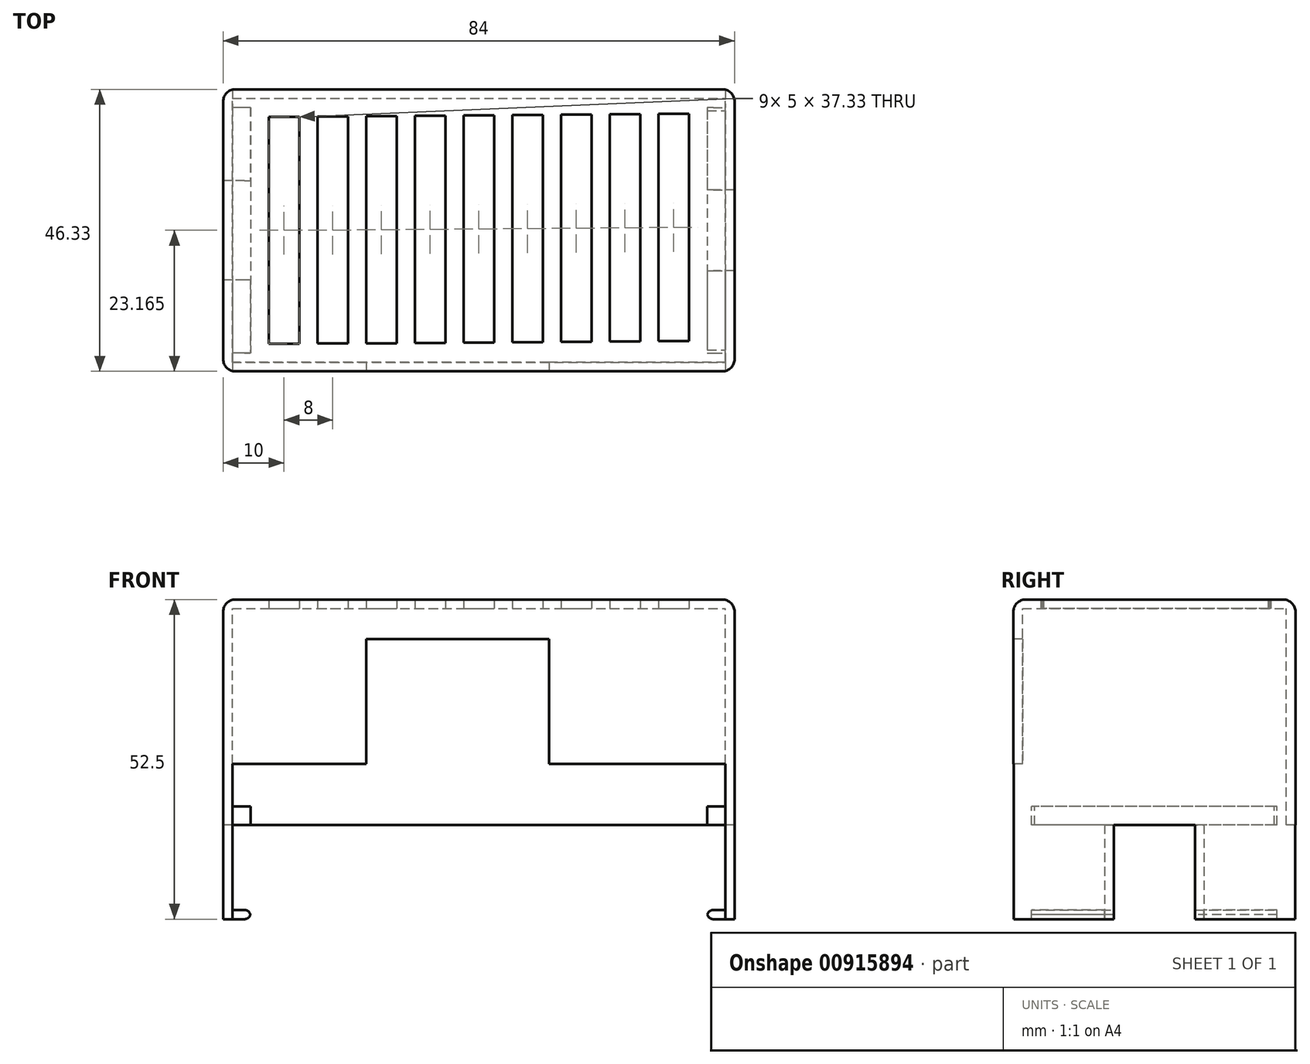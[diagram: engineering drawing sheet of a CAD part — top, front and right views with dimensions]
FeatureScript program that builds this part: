
annotation { "Feature Type Name" : "Feature", "Feature Type Description" : "" }
export const myFeature = defineFeature(function(context is Context, id is Id, definition is map)
    precondition{}
    {
        {
            var Q0;
            Q0=qCreatedBy(makeId("Top.planeOp"),FACE);
            var sketch = newSketch(context, id + "F0", { "sketchPlane" : qUnion([Q0])});
            skLineSegment(sketch, "E0.bottom", {"start": v(0, 0) * mm, "end": v(84, 0) * mm});
            skLineSegment(sketch, "E0.top", {"start": v(0, 46.33) * mm, "end": v(84, 46.33) * mm});
            skLineSegment(sketch, "E0.left", {"start": v(0, 0) * mm, "end": v(0, 46.33) * mm});
            skLineSegment(sketch, "E0.right", {"start": v(84, 0) * mm, "end": v(84, 46.33) * mm});
            skSolve(sketch);
        }
        {
            var Q0;
            Q0=makeQuery(id+"F0.imprint","IMPRINT",FACE,{"disambiguationData":[TD([[makeQuery(id+"F0.imprint","IMPRINT",EDGE,{"derivedFrom":sQuery(id+"F0.wireOp",EDGE,"E0.bottom")}),1.0]])]});
            extrude(context, id + "F1", {"entities" : qUnion([Q0]), "oppositeDirection" : true, "depth" : 37 * mm, "offsetDistance" : 25 * mm});
        }
        {
            var Q0;
            Q0=makeQuery(id+"F1.opExtrude","CAP_FACE",FACE,{"disambiguationData":[OSD([sQuery(id+"F0.wireOp",EDGE,"E0.bottom"),sQuery(id+"F0.wireOp",EDGE,"E0.top"),sQuery(id+"F0.wireOp",EDGE,"E0.left"),sQuery(id+"F0.wireOp",EDGE,"E0.right")])],"isStart":false});
            shell(context, id + "F2", {"entities" : qUnion([Q0]), "thickness" : 1.5 * mm});
        }
        {
            var Q0;
            Q0=makeQuery(id+"F1.opExtrude","SWEPT_FACE",FACE,{"disambiguationData":[OSD([sQuery(id+"F0.wireOp",EDGE,"E0.top")])]});
            var sketch = newSketch(context, id + "F3", { "sketchPlane" : qUnion([Q0])});
            skLineSegment(sketch, "E1.bottom", {"start": v(-82.5, -37) * mm, "end": v(-1.5, -37) * mm});
            skLineSegment(sketch, "E1.top", {"start": v(-82.5, -1.5) * mm, "end": v(-1.5, -1.5) * mm});
            skLineSegment(sketch, "E1.left", {"start": v(-82.5, -37) * mm, "end": v(-82.5, -1.5) * mm});
            skLineSegment(sketch, "E1.right", {"start": v(-1.5, -37) * mm, "end": v(-1.5, -1.5) * mm});
            skSolve(sketch);
        }
        {
            var Q0;
            Q0=makeQuery(id+"F1.opExtrude","SWEPT_FACE",FACE,{"disambiguationData":[OSD([sQuery(id+"F0.wireOp",EDGE,"E0.bottom")])]});
            var sketch = newSketch(context, id + "F4", { "sketchPlane" : qUnion([Q0])});
            skLineSegment(sketch, "E2.bottom", {"start": v(1.5, -37) * mm, "end": v(82.5, -37) * mm});
            skLineSegment(sketch, "E2.top", {"start": v(1.5, -27) * mm, "end": v(82.5, -27) * mm});
            skLineSegment(sketch, "E2.left", {"start": v(1.5, -37) * mm, "end": v(1.5, -27) * mm});
            skLineSegment(sketch, "E2.right", {"start": v(82.5, -37) * mm, "end": v(82.5, -27) * mm});
            skSolve(sketch);
        }
        {
            var Q0;
            Q0=makeQuery(id+"F4.imprint","IMPRINT",FACE,{"disambiguationData":[TD([[makeQuery(id+"F4.imprint","IMPRINT",EDGE,{"derivedFrom":sQuery(id+"F4.wireOp",EDGE,"E2.bottom")}),1.0]])]});
            extrude(context, id + "F5", {"entities" : qUnion([Q0]), "operationType" : NewBodyOperationType.REMOVE, "endBound" : BoundingType.UP_TO_NEXT, "oppositeDirection" : true, "depth" : 25 * mm, "offsetDistance" : 25 * mm});
        }
        {
            var Q0;
            Q0=makeQuery(id+"F1.opExtrude","SWEPT_FACE",FACE,{"disambiguationData":[OSD([sQuery(id+"F0.wireOp",EDGE,"E0.bottom")])]});
            var sketch = newSketch(context, id + "F6", { "sketchPlane" : qUnion([Q0])});
            skLineSegment(sketch, "E3.bottom", {"start": v(23.5, -27) * mm, "end": v(53.5, -27) * mm});
            skLineSegment(sketch, "E3.top", {"start": v(23.5, -6.5) * mm, "end": v(53.5, -6.5) * mm});
            skLineSegment(sketch, "E3.left", {"start": v(23.5, -27) * mm, "end": v(23.5, -6.5) * mm});
            skLineSegment(sketch, "E3.right", {"start": v(53.5, -27) * mm, "end": v(53.5, -6.5) * mm});
            skSolve(sketch);
        }
        {
            var Q0;
            Q0=makeQuery(id+"F6.imprint","IMPRINT",FACE,{"disambiguationData":[TD([[makeQuery(id+"F6.imprint","IMPRINT",EDGE,{"derivedFrom":sQuery(id+"F6.wireOp",EDGE,"E3.bottom")}),1.0]])]});
            extrude(context, id + "F7", {"entities" : qUnion([Q0]), "operationType" : NewBodyOperationType.REMOVE, "endBound" : BoundingType.UP_TO_NEXT, "oppositeDirection" : true, "depth" : 25 * mm, "offsetDistance" : 25 * mm});
        }
        {
            var Q0;
            Q0=makeQuery(id+"F1.opExtrude","CAP_FACE",FACE,{"disambiguationData":[OSD([sQuery(id+"F0.wireOp",EDGE,"E0.bottom"),sQuery(id+"F0.wireOp",EDGE,"E0.top"),sQuery(id+"F0.wireOp",EDGE,"E0.left"),sQuery(id+"F0.wireOp",EDGE,"E0.right")])],"isStart":false});
            var sketch = newSketch(context, id + "F8", { "sketchPlane" : qUnion([Q0])});
            skLineSegment(sketch, "E4.bottom", {"start": v(0, -46.33) * mm, "end": v(1.5, -46.33) * mm});
            skLineSegment(sketch, "E4.top", {"start": v(0, 0) * mm, "end": v(1.5, 0) * mm});
            skLineSegment(sketch, "E4.left", {"start": v(0, -46.33) * mm, "end": v(0, 0) * mm});
            skLineSegment(sketch, "E4.right", {"start": v(1.5, -46.33) * mm, "end": v(1.5, 0) * mm});
            skLineSegment(sketch, "E5.bottom", {"start": v(84, -46.33) * mm, "end": v(82.5, -46.33) * mm});
            skLineSegment(sketch, "E5.top", {"start": v(84, 0) * mm, "end": v(82.5, 0) * mm});
            skLineSegment(sketch, "E5.left", {"start": v(84, -46.33) * mm, "end": v(84, 0) * mm});
            skLineSegment(sketch, "E5.right", {"start": v(82.5, -46.33) * mm, "end": v(82.5, 0) * mm});
            skSolve(sketch);
        }
        {
            var Q0;
            {var subQ4=sQuery(id+"F8.wireOp",EDGE,"E4.bottom");Q0=makeQuery(id+"F8.imprint","IMPRINT",FACE,{"disambiguationData":[TD([[makeQuery(id+"F8.imprint","IMPRINT",EDGE,{"derivedFrom":subQ4}),1.0]])]});}
            var Q1;
            {var subQ4=sQuery(id+"F8.wireOp",EDGE,"E5.bottom");Q1=makeQuery(id+"F8.imprint","IMPRINT",FACE,{"disambiguationData":[TD([[makeQuery(id+"F8.imprint","IMPRINT",EDGE,{"derivedFrom":subQ4}),1.0]])]});}
            extrude(context, id + "F9", {"entities" : qUnion([Q0, Q1]), "operationType" : NewBodyOperationType.ADD, "depth" : 15.5 * mm, "offsetDistance" : 25 * mm});
        }
        {
            var Q0;
            Q0=makeQuery(id+"F9.boolean.opBoolean","MERGE",FACE,{"derivedFrom":[makeQuery(id+"F5.boolean.opBoolean","MERGE",FACE,{"derivedFrom":[makeQuery(id+"F2.opShell","OFFSET_FACE",FACE,{"disambiguationData":[OSD([sQuery(id+"F0.wireOp",EDGE,"E0.left")])]})],"fromTools":[makeQuery(id+"F5.opExtrude","SWEPT_FACE",FACE,{"disambiguationData":[OSD([sQuery(id+"F4.wireOp",EDGE,"E2.left")])]})]}),makeQuery(id+"F9.opExtrude","SWEPT_FACE",FACE,{"disambiguationData":[OSD([sQuery(id+"F8.wireOp",EDGE,"E4.right")])]})]});
            var sketch = newSketch(context, id + "F10", { "sketchPlane" : qUnion([Q0])});
            skLineSegment(sketch, "E6.bottom", {"start": v(43.33, -37) * mm, "end": v(3, -37) * mm});
            skLineSegment(sketch, "E6.top", {"start": v(43.33, -34) * mm, "end": v(3, -34) * mm});
            skLineSegment(sketch, "E6.left", {"start": v(43.33, -37) * mm, "end": v(43.33, -34) * mm});
            skLineSegment(sketch, "E6.right", {"start": v(3, -37) * mm, "end": v(3, -34) * mm});
            skSolve(sketch);
        }
        {
            var Q0;
            Q0=makeQuery(id+"F10.imprint","IMPRINT",FACE,{"disambiguationData":[TD([[makeQuery(id+"F10.imprint","IMPRINT",EDGE,{"derivedFrom":sQuery(id+"F10.wireOp",EDGE,"E6.bottom")}),-1.0]])]});
            extrude(context, id + "F11", {"entities" : qUnion([Q0]), "operationType" : NewBodyOperationType.ADD, "depth" : 3 * mm, "offsetDistance" : 25 * mm});
        }
        {
            var Q0;
            Q0=makeQuery(id+"F9.boolean.opBoolean","MERGE",FACE,{"derivedFrom":[makeQuery(id+"F5.boolean.opBoolean","MERGE",FACE,{"derivedFrom":[makeQuery(id+"F2.opShell","OFFSET_FACE",FACE,{"disambiguationData":[OSD([sQuery(id+"F0.wireOp",EDGE,"E0.right")])]})],"fromTools":[makeQuery(id+"F5.opExtrude","SWEPT_FACE",FACE,{"disambiguationData":[OSD([sQuery(id+"F4.wireOp",EDGE,"E2.right")])]})]}),makeQuery(id+"F9.opExtrude","SWEPT_FACE",FACE,{"disambiguationData":[OSD([sQuery(id+"F8.wireOp",EDGE,"E5.right")])]})]});
            var sketch = newSketch(context, id + "F12", { "sketchPlane" : qUnion([Q0])});
            skLineSegment(sketch, "E7.bottom", {"start": v(-42.83, -37) * mm, "end": v(-3.5, -37) * mm});
            skLineSegment(sketch, "E7.top", {"start": v(-42.83, -34) * mm, "end": v(-3.5, -34) * mm});
            skLineSegment(sketch, "E7.left", {"start": v(-42.83, -37) * mm, "end": v(-42.83, -34) * mm});
            skLineSegment(sketch, "E7.right", {"start": v(-3.5, -37) * mm, "end": v(-3.5, -34) * mm});
            skSolve(sketch);
        }
        {
            var Q0;
            Q0=makeQuery(id+"F12.imprint","IMPRINT",FACE,{"disambiguationData":[TD([[makeQuery(id+"F12.imprint","IMPRINT",EDGE,{"derivedFrom":sQuery(id+"F12.wireOp",EDGE,"E7.bottom")}),1.0]])]});
            extrude(context, id + "F13", {"entities" : qUnion([Q0]), "operationType" : NewBodyOperationType.ADD, "depth" : 3 * mm, "offsetDistance" : 25 * mm});
        }
        {
            var Q0;
            Q0=makeQuery(id+"F9.opExtrude","CAP_FACE",FACE,{"disambiguationData":[OSD([sQuery(id+"F8.wireOp",EDGE,"E5.bottom"),sQuery(id+"F8.wireOp",EDGE,"E5.top"),sQuery(id+"F8.wireOp",EDGE,"E5.left"),sQuery(id+"F8.wireOp",EDGE,"E5.right")])],"isStart":false});
            var sketch = newSketch(context, id + "F14", { "sketchPlane" : qUnion([Q0])});
            skLineSegment(sketch, "E8.bottom", {"start": v(84, -29.83) * mm, "end": v(82.5, -29.83) * mm});
            skLineSegment(sketch, "E8.top", {"start": v(84, -16.5) * mm, "end": v(82.5, -16.5) * mm});
            skLineSegment(sketch, "E8.left", {"start": v(84, -29.83) * mm, "end": v(84, -16.5) * mm});
            skLineSegment(sketch, "E8.right", {"start": v(82.5, -29.83) * mm, "end": v(82.5, -16.5) * mm});
            skSolve(sketch);
        }
        {
            var Q0;
            Q0=makeQuery(id+"F14.imprint","IMPRINT",FACE,{"disambiguationData":[TD([[makeQuery(id+"F14.imprint","IMPRINT",EDGE,{"derivedFrom":sQuery(id+"F14.wireOp",EDGE,"E8.bottom")}),-1.0]])]});
            extrude(context, id + "F15", {"entities" : qUnion([Q0]), "operationType" : NewBodyOperationType.REMOVE, "oppositeDirection" : true, "depth" : 15.5 * mm, "offsetDistance" : 25 * mm});
        }
        {
            var Q0;
            Q0=makeQuery(id+"F9.opExtrude","CAP_FACE",FACE,{"disambiguationData":[OSD([sQuery(id+"F8.wireOp",EDGE,"E4.bottom"),sQuery(id+"F8.wireOp",EDGE,"E4.top"),sQuery(id+"F8.wireOp",EDGE,"E4.left"),sQuery(id+"F8.wireOp",EDGE,"E4.right")])],"isStart":false});
            var sketch = newSketch(context, id + "F16", { "sketchPlane" : qUnion([Q0])});
            skLineSegment(sketch, "E9.bottom", {"start": v(1.5, -31.33) * mm, "end": v(0, -31.33) * mm});
            skLineSegment(sketch, "E9.top", {"start": v(1.5, -15) * mm, "end": v(0, -15) * mm});
            skLineSegment(sketch, "E9.left", {"start": v(1.5, -31.33) * mm, "end": v(1.5, -15) * mm});
            skLineSegment(sketch, "E9.right", {"start": v(0, -31.33) * mm, "end": v(0, -15) * mm});
            skSolve(sketch);
        }
        {
            var Q0;
            Q0=makeQuery(id+"F16.imprint","IMPRINT",FACE,{"disambiguationData":[TD([[makeQuery(id+"F16.imprint","IMPRINT",EDGE,{"derivedFrom":sQuery(id+"F16.wireOp",EDGE,"E9.bottom")}),-1.0]])]});
            extrude(context, id + "F17", {"entities" : qUnion([Q0]), "operationType" : NewBodyOperationType.REMOVE, "oppositeDirection" : true, "depth" : 15.5 * mm, "offsetDistance" : 25 * mm});
        }
        {
            var Q0;
            Q0=makeQuery(id+"F9.boolean.opBoolean","MERGE",FACE,{"derivedFrom":[makeQuery(id+"F5.boolean.opBoolean","MERGE",FACE,{"derivedFrom":[makeQuery(id+"F2.opShell","OFFSET_FACE",FACE,{"disambiguationData":[OSD([sQuery(id+"F0.wireOp",EDGE,"E0.left")])]})],"fromTools":[makeQuery(id+"F5.opExtrude","SWEPT_FACE",FACE,{"disambiguationData":[OSD([sQuery(id+"F4.wireOp",EDGE,"E2.left")])]})]}),makeQuery(id+"F9.opExtrude","SWEPT_FACE",FACE,{"disambiguationData":[OSD([sQuery(id+"F8.wireOp",EDGE,"E4.right")])]})]});
            var sketch = newSketch(context, id + "F18", { "sketchPlane" : qUnion([Q0])});
            skLineSegment(sketch, "E10.bottom", {"start": v(43.33, -52.5) * mm, "end": v(31.33, -52.5) * mm});
            skLineSegment(sketch, "E10.top", {"start": v(43.33, -51) * mm, "end": v(31.33, -51) * mm});
            skLineSegment(sketch, "E10.left", {"start": v(43.33, -52.5) * mm, "end": v(43.33, -51) * mm});
            skLineSegment(sketch, "E10.right", {"start": v(3, -52.5) * mm, "end": v(3, -51) * mm});
            skLineSegment(sketch, "E11", {"start": v(31.33, -52.5) * mm, "end": v(31.33, -51) * mm});
            skLineSegment(sketch, "E12", {"start": v(15, -52.5) * mm, "end": v(15, -51) * mm});
            skLineSegment(sketch, "E13.trimOffspring", {"start": v(15, -52.5) * mm, "end": v(3, -52.5) * mm});
            skLineSegment(sketch, "E14.trimOffspring", {"start": v(15, -51) * mm, "end": v(3, -51) * mm});
            skSolve(sketch);
        }
        {
            var Q0;
            Q0=makeQuery(id+"F18.imprint","IMPRINT",FACE,{"disambiguationData":[TD([[makeQuery(id+"F18.imprint","IMPRINT",EDGE,{"derivedFrom":sQuery(id+"F18.wireOp",EDGE,"E10.bottom")}),-1.0]])]});
            var Q1;
            Q1=makeQuery(id+"F18.imprint","IMPRINT",FACE,{"disambiguationData":[TD([[makeQuery(id+"F18.imprint","IMPRINT",EDGE,{"derivedFrom":sQuery(id+"F18.wireOp",EDGE,"E10.right")}),-1.0]])]});
            extrude(context, id + "F19", {"entities" : qUnion([Q0, Q1]), "operationType" : NewBodyOperationType.ADD, "depth" : 3 * mm, "offsetDistance" : 25 * mm});
        }
        {
            var Q0;
            Q0=makeQuery(id+"F9.boolean.opBoolean","MERGE",FACE,{"derivedFrom":[makeQuery(id+"F5.boolean.opBoolean","MERGE",FACE,{"derivedFrom":[makeQuery(id+"F2.opShell","OFFSET_FACE",FACE,{"disambiguationData":[OSD([sQuery(id+"F0.wireOp",EDGE,"E0.right")])]})],"fromTools":[makeQuery(id+"F5.opExtrude","SWEPT_FACE",FACE,{"disambiguationData":[OSD([sQuery(id+"F4.wireOp",EDGE,"E2.right")])]})]}),makeQuery(id+"F9.opExtrude","SWEPT_FACE",FACE,{"disambiguationData":[OSD([sQuery(id+"F8.wireOp",EDGE,"E5.right")])]})]});
            var sketch = newSketch(context, id + "F20", { "sketchPlane" : qUnion([Q0])});
            skLineSegment(sketch, "E15.bottom", {"start": v(-3, -52.5) * mm, "end": v(-16.5, -52.5) * mm});
            skLineSegment(sketch, "E15.top", {"start": v(-3, -51) * mm, "end": v(-16.5, -51) * mm});
            skLineSegment(sketch, "E15.left", {"start": v(-3, -52.5) * mm, "end": v(-3, -51) * mm});
            skLineSegment(sketch, "E15.right", {"start": v(-43.33, -52.5) * mm, "end": v(-43.33, -51) * mm});
            skLineSegment(sketch, "E16", {"start": v(-16.5, -52.5) * mm, "end": v(-16.5, -51) * mm});
            skLineSegment(sketch, "E17", {"start": v(-29.83, -52.5) * mm, "end": v(-29.83, -51) * mm});
            skLineSegment(sketch, "E18.trimOffspring", {"start": v(-29.83, -52.5) * mm, "end": v(-43.33, -52.5) * mm});
            skLineSegment(sketch, "E19.trimOffspring", {"start": v(-29.83, -51) * mm, "end": v(-43.33, -51) * mm});
            skSolve(sketch);
        }
        {
            var Q0;
            Q0=makeQuery(id+"F20.imprint","IMPRINT",FACE,{"disambiguationData":[TD([[makeQuery(id+"F20.imprint","IMPRINT",EDGE,{"derivedFrom":sQuery(id+"F20.wireOp",EDGE,"E15.bottom")}),1.0]])]});
            var Q1;
            Q1=makeQuery(id+"F20.imprint","IMPRINT",FACE,{"disambiguationData":[TD([[makeQuery(id+"F20.imprint","IMPRINT",EDGE,{"derivedFrom":sQuery(id+"F20.wireOp",EDGE,"E15.right")}),-1.0]])]});
            extrude(context, id + "F21", {"entities" : qUnion([Q0, Q1]), "operationType" : NewBodyOperationType.ADD, "depth" : 3 * mm, "offsetDistance" : 25 * mm});
        }
        {
            var Q0;
            Q0=makeQuery(id+"F2.opShell","OFFSET_FACE",FACE,{"disambiguationData":[OSD([sQuery(id+"F0.wireOp",EDGE,"E0.bottom"),sQuery(id+"F0.wireOp",EDGE,"E0.top"),sQuery(id+"F0.wireOp",EDGE,"E0.left"),sQuery(id+"F0.wireOp",EDGE,"E0.right")])]});
            var sketch = newSketch(context, id + "F22", { "sketchPlane" : qUnion([Q0])});
            skLineSegment(sketch, "E20.bottom", {"start": v(7.5, -41.83) * mm, "end": v(12.5, -41.83) * mm});
            skLineSegment(sketch, "E20.top", {"start": v(7.5, -4.5) * mm, "end": v(12.5, -4.5) * mm});
            skLineSegment(sketch, "E20.left", {"start": v(7.5, -41.83) * mm, "end": v(7.5, -4.5) * mm});
            skLineSegment(sketch, "E20.right", {"start": v(12.5, -41.83) * mm, "end": v(12.5, -4.5) * mm});
            skLineSegment(sketch, "E21.1.0.0", {"start": v(20.5, -41.89) * mm, "end": v(20.5, -4.56) * mm});
            skLineSegment(sketch, "E21.1.0.1", {"start": v(15.5, -4.56) * mm, "end": v(20.5, -4.56) * mm});
            skLineSegment(sketch, "E21.1.0.2", {"start": v(15.5, -41.89) * mm, "end": v(15.5, -4.56) * mm});
            skLineSegment(sketch, "E21.1.0.3", {"start": v(15.5, -41.89) * mm, "end": v(20.5, -41.89) * mm});
            skLineSegment(sketch, "E21.2.0.0", {"start": v(28.5, -41.95) * mm, "end": v(28.5, -4.62) * mm});
            skLineSegment(sketch, "E21.2.0.1", {"start": v(23.5, -4.62) * mm, "end": v(28.5, -4.62) * mm});
            skLineSegment(sketch, "E21.2.0.2", {"start": v(23.5, -41.95) * mm, "end": v(23.5, -4.62) * mm});
            skLineSegment(sketch, "E21.2.0.3", {"start": v(23.5, -41.95) * mm, "end": v(28.5, -41.95) * mm});
            skLineSegment(sketch, "E21.3.0.0", {"start": v(36.5, -42) * mm, "end": v(36.5, -4.68) * mm});
            skLineSegment(sketch, "E21.3.0.1", {"start": v(31.5, -4.68) * mm, "end": v(36.5, -4.68) * mm});
            skLineSegment(sketch, "E21.3.0.2", {"start": v(31.5, -42) * mm, "end": v(31.5, -4.68) * mm});
            skLineSegment(sketch, "E21.3.0.3", {"start": v(31.5, -42) * mm, "end": v(36.5, -42) * mm});
            skLineSegment(sketch, "E21.4.0.0", {"start": v(44.5, -42.07) * mm, "end": v(44.5, -4.74) * mm});
            skLineSegment(sketch, "E21.4.0.1", {"start": v(39.5, -4.74) * mm, "end": v(44.5, -4.74) * mm});
            skLineSegment(sketch, "E21.4.0.2", {"start": v(39.5, -42.07) * mm, "end": v(39.5, -4.74) * mm});
            skLineSegment(sketch, "E21.4.0.3", {"start": v(39.5, -42.07) * mm, "end": v(44.5, -42.07) * mm});
            skLineSegment(sketch, "E21.5.0.0", {"start": v(52.5, -42.13) * mm, "end": v(52.5, -4.8) * mm});
            skLineSegment(sketch, "E21.5.0.1", {"start": v(47.5, -4.8) * mm, "end": v(52.5, -4.8) * mm});
            skLineSegment(sketch, "E21.5.0.2", {"start": v(47.5, -42.13) * mm, "end": v(47.5, -4.8) * mm});
            skLineSegment(sketch, "E21.5.0.3", {"start": v(47.5, -42.13) * mm, "end": v(52.5, -42.13) * mm});
            skLineSegment(sketch, "E21.6.0.0", {"start": v(60.5, -42.19) * mm, "end": v(60.5, -4.86) * mm});
            skLineSegment(sketch, "E21.6.0.1", {"start": v(55.5, -4.86) * mm, "end": v(60.5, -4.86) * mm});
            skLineSegment(sketch, "E21.6.0.2", {"start": v(55.5, -42.19) * mm, "end": v(55.5, -4.86) * mm});
            skLineSegment(sketch, "E21.6.0.3", {"start": v(55.5, -42.19) * mm, "end": v(60.5, -42.19) * mm});
            skLineSegment(sketch, "E21.7.0.0", {"start": v(68.5, -42.25) * mm, "end": v(68.5, -4.92) * mm});
            skLineSegment(sketch, "E21.7.0.1", {"start": v(63.5, -4.92) * mm, "end": v(68.5, -4.92) * mm});
            skLineSegment(sketch, "E21.7.0.2", {"start": v(63.5, -42.25) * mm, "end": v(63.5, -4.92) * mm});
            skLineSegment(sketch, "E21.7.0.3", {"start": v(63.5, -42.25) * mm, "end": v(68.5, -42.25) * mm});
            skLineSegment(sketch, "E21.8.0.0", {"start": v(76.5, -42.3) * mm, "end": v(76.5, -4.98) * mm});
            skLineSegment(sketch, "E21.8.0.1", {"start": v(71.5, -4.98) * mm, "end": v(76.5, -4.98) * mm});
            skLineSegment(sketch, "E21.8.0.2", {"start": v(71.5, -42.3) * mm, "end": v(71.5, -4.98) * mm});
            skLineSegment(sketch, "E21.8.0.3", {"start": v(71.5, -42.3) * mm, "end": v(76.5, -42.3) * mm});
            skLineSegment(sketch, "E21.direction1", {"start": v(7.5, -41.83) * mm, "end": v(15.5, -41.89) * mm, "construction": true});
            skSolve(sketch);
        }
        {
            var Q0;
            Q0=makeQuery(id+"F22.imprint","IMPRINT",FACE,{"disambiguationData":[TD([[makeQuery(id+"F22.imprint","IMPRINT",EDGE,{"derivedFrom":sQuery(id+"F22.wireOp",EDGE,"E21.8.0.0")}),1.0]])]});
            var Q1;
            Q1=makeQuery(id+"F22.imprint","IMPRINT",FACE,{"disambiguationData":[TD([[makeQuery(id+"F22.imprint","IMPRINT",EDGE,{"derivedFrom":sQuery(id+"F22.wireOp",EDGE,"E21.7.0.0")}),1.0]])]});
            var Q2;
            Q2=makeQuery(id+"F22.imprint","IMPRINT",FACE,{"disambiguationData":[TD([[makeQuery(id+"F22.imprint","IMPRINT",EDGE,{"derivedFrom":sQuery(id+"F22.wireOp",EDGE,"E21.5.0.0")}),1.0]])]});
            var Q3;
            Q3=makeQuery(id+"F22.imprint","IMPRINT",FACE,{"disambiguationData":[TD([[makeQuery(id+"F22.imprint","IMPRINT",EDGE,{"derivedFrom":sQuery(id+"F22.wireOp",EDGE,"E21.4.0.0")}),1.0]])]});
            var Q4;
            Q4=makeQuery(id+"F22.imprint","IMPRINT",FACE,{"disambiguationData":[TD([[makeQuery(id+"F22.imprint","IMPRINT",EDGE,{"derivedFrom":sQuery(id+"F22.wireOp",EDGE,"E21.3.0.0")}),1.0]])]});
            var Q5;
            Q5=makeQuery(id+"F22.imprint","IMPRINT",FACE,{"disambiguationData":[TD([[makeQuery(id+"F22.imprint","IMPRINT",EDGE,{"derivedFrom":sQuery(id+"F22.wireOp",EDGE,"E21.2.0.0")}),1.0]])]});
            var Q6;
            Q6=makeQuery(id+"F22.imprint","IMPRINT",FACE,{"disambiguationData":[TD([[makeQuery(id+"F22.imprint","IMPRINT",EDGE,{"derivedFrom":sQuery(id+"F22.wireOp",EDGE,"E21.1.0.0")}),1.0]])]});
            var Q7;
            Q7=makeQuery(id+"F22.imprint","IMPRINT",FACE,{"disambiguationData":[TD([[makeQuery(id+"F22.imprint","IMPRINT",EDGE,{"derivedFrom":sQuery(id+"F22.wireOp",EDGE,"E20.bottom")}),1.0]])]});
            var Q8;
            Q8=makeQuery(id+"F22.imprint","IMPRINT",FACE,{"disambiguationData":[TD([[makeQuery(id+"F22.imprint","IMPRINT",EDGE,{"derivedFrom":sQuery(id+"F22.wireOp",EDGE,"E21.6.0.0")}),1.0]])]});
            extrude(context, id + "F23", {"entities" : qUnion([Q0, Q1, Q2, Q3, Q4, Q5, Q6, Q7, Q8]), "operationType" : NewBodyOperationType.REMOVE, "endBound" : BoundingType.UP_TO_NEXT, "oppositeDirection" : true, "depth" : 25 * mm, "offsetDistance" : 25 * mm});
        }
        {
            var Q0;
            Q0=makeQuery(id+"F1.opExtrude","CAP_EDGE",EDGE,{"disambiguationData":[OSD([sQuery(id+"F0.wireOp",EDGE,"E0.bottom")])],"isStart":true});
            var Q1;
            Q1=makeQuery(id+"F1.opExtrude","CAP_EDGE",EDGE,{"disambiguationData":[OSD([sQuery(id+"F0.wireOp",EDGE,"E0.right")])],"isStart":true});
            var Q2;
            Q2=makeQuery(id+"F9.boolean.opBoolean","MERGE",EDGE,{"derivedFrom":[makeQuery(id+"F1.opExtrude","SWEPT_EDGE",EDGE,{"disambiguationData":[OSD([sQuery(id+"F0.wireOp",EDGE,"E0.bottom"),sQuery(id+"F0.wireOp",EDGE,"E0.right")])]}),makeQuery(id+"F9.opExtrude","SWEPT_EDGE",EDGE,{"disambiguationData":[OSD([sQuery(id+"F8.wireOp",EDGE,"E5.top"),sQuery(id+"F8.wireOp",EDGE,"E5.left")])]})]});
            var Q3;
            Q3=makeQuery(id+"F9.boolean.opBoolean","MERGE",EDGE,{"derivedFrom":[makeQuery(id+"F1.opExtrude","SWEPT_EDGE",EDGE,{"disambiguationData":[OSD([sQuery(id+"F0.wireOp",EDGE,"E0.top"),sQuery(id+"F0.wireOp",EDGE,"E0.right")])]}),makeQuery(id+"F9.opExtrude","SWEPT_EDGE",EDGE,{"disambiguationData":[OSD([sQuery(id+"F8.wireOp",EDGE,"E5.bottom"),sQuery(id+"F8.wireOp",EDGE,"E5.left")])]})]});
            var Q4;
            Q4=makeQuery(id+"F1.opExtrude","CAP_EDGE",EDGE,{"disambiguationData":[OSD([sQuery(id+"F0.wireOp",EDGE,"E0.top")])],"isStart":true});
            var Q5;
            Q5=makeQuery(id+"F9.boolean.opBoolean","MERGE",EDGE,{"derivedFrom":[makeQuery(id+"F1.opExtrude","SWEPT_EDGE",EDGE,{"disambiguationData":[OSD([sQuery(id+"F0.wireOp",EDGE,"E0.top"),sQuery(id+"F0.wireOp",EDGE,"E0.left")])]}),makeQuery(id+"F9.opExtrude","SWEPT_EDGE",EDGE,{"disambiguationData":[OSD([sQuery(id+"F8.wireOp",EDGE,"E4.bottom"),sQuery(id+"F8.wireOp",EDGE,"E4.left")])]})]});
            var Q6;
            Q6=makeQuery(id+"F1.opExtrude","CAP_EDGE",EDGE,{"disambiguationData":[OSD([sQuery(id+"F0.wireOp",EDGE,"E0.left")])],"isStart":true});
            var Q7;
            Q7=makeQuery(id+"F9.boolean.opBoolean","MERGE",EDGE,{"derivedFrom":[makeQuery(id+"F1.opExtrude","SWEPT_EDGE",EDGE,{"disambiguationData":[OSD([sQuery(id+"F0.wireOp",EDGE,"E0.bottom"),sQuery(id+"F0.wireOp",EDGE,"E0.left")])]}),makeQuery(id+"F9.opExtrude","SWEPT_EDGE",EDGE,{"disambiguationData":[OSD([sQuery(id+"F8.wireOp",EDGE,"E4.top"),sQuery(id+"F8.wireOp",EDGE,"E4.left")])]})]});
            fillet(context, id + "F24", {"entities" : qUnion([Q0, Q1, Q2, Q3, Q4, Q5, Q6, Q7]), "radius" : 2 * mm, "tangentPropagation" : true, "allowEdgeOverflow" : false});
        }
        {
            var Q0;
            Q0=makeQuery(id+"F19.opExtrude","CAP_EDGE",EDGE,{"disambiguationData":[OSD([sQuery(id+"F18.wireOp",EDGE,"E13.trimOffspring")])],"isStart":false});
            var Q1;
            Q1=makeQuery(id+"F19.opExtrude","CAP_EDGE",EDGE,{"disambiguationData":[OSD([sQuery(id+"F18.wireOp",EDGE,"E14.trimOffspring")])],"isStart":false});
            var Q2;
            Q2=makeQuery(id+"F19.opExtrude","CAP_EDGE",EDGE,{"disambiguationData":[OSD([sQuery(id+"F18.wireOp",EDGE,"E10.bottom")])],"isStart":false});
            var Q3;
            Q3=makeQuery(id+"F19.opExtrude","CAP_EDGE",EDGE,{"disambiguationData":[OSD([sQuery(id+"F18.wireOp",EDGE,"E10.top")])],"isStart":false});
            var Q4;
            Q4=makeQuery(id+"F21.opExtrude","CAP_EDGE",EDGE,{"disambiguationData":[OSD([sQuery(id+"F20.wireOp",EDGE,"E15.top")])],"isStart":false});
            var Q5;
            Q5=makeQuery(id+"F21.opExtrude","CAP_EDGE",EDGE,{"disambiguationData":[OSD([sQuery(id+"F20.wireOp",EDGE,"E15.bottom")])],"isStart":false});
            var Q6;
            Q6=makeQuery(id+"F21.opExtrude","CAP_EDGE",EDGE,{"disambiguationData":[OSD([sQuery(id+"F20.wireOp",EDGE,"E18.trimOffspring")])],"isStart":false});
            var Q7;
            Q7=makeQuery(id+"F21.opExtrude","CAP_EDGE",EDGE,{"disambiguationData":[OSD([sQuery(id+"F20.wireOp",EDGE,"E19.trimOffspring")])],"isStart":false});
            fillet(context, id + "F25", {"entities" : qUnion([Q0, Q1, Q2, Q3, Q4, Q5, Q6, Q7]), "radius" : 1 * mm, "tangentPropagation" : true, "allowEdgeOverflow" : false});
        }
    });
